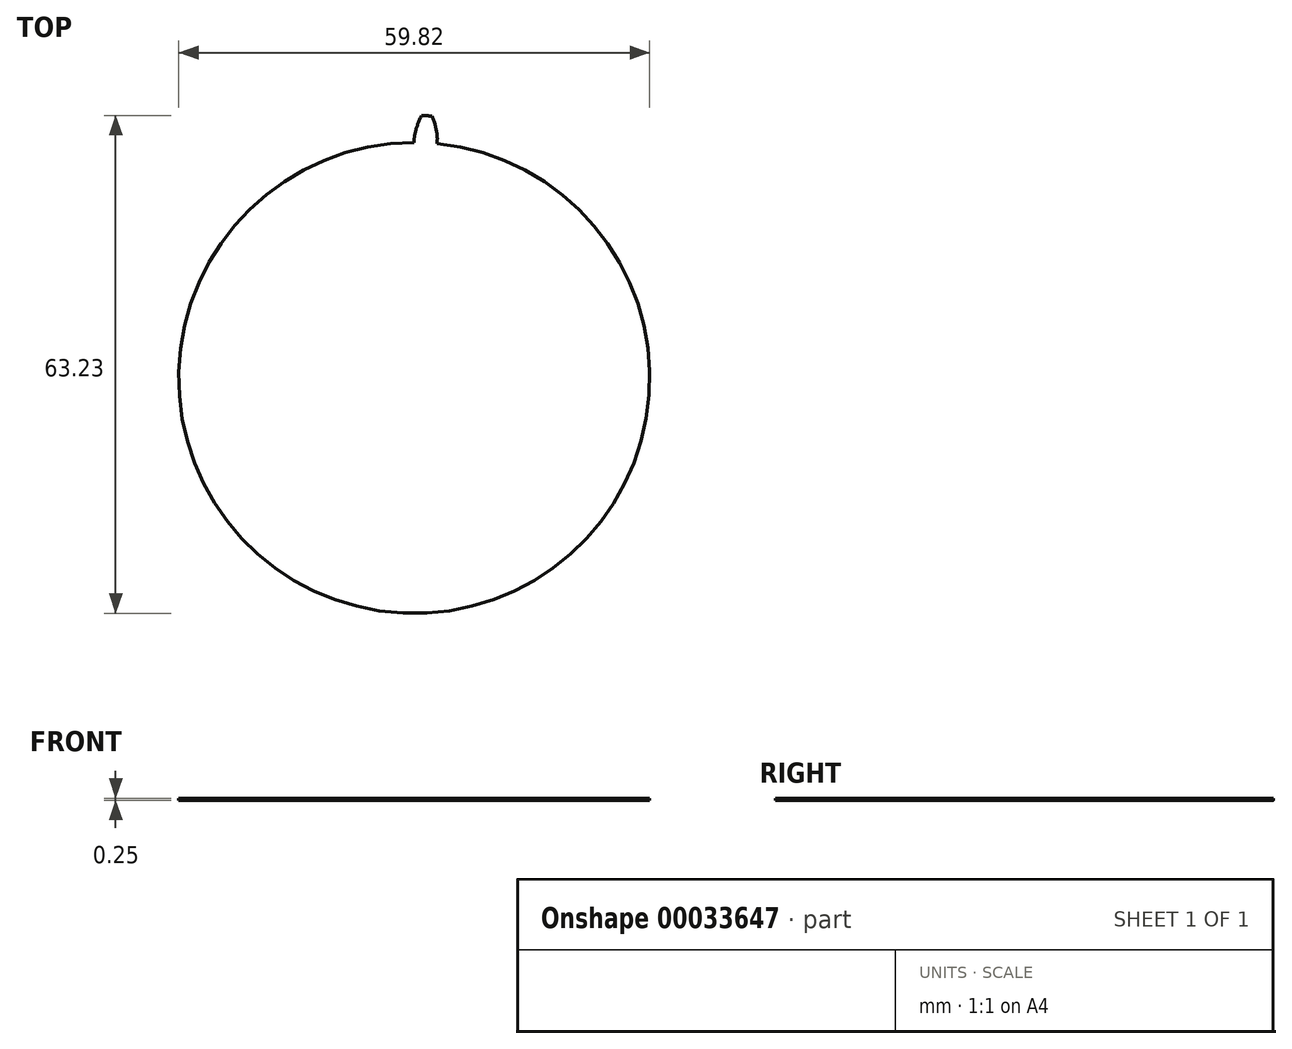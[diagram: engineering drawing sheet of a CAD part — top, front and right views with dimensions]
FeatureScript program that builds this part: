
annotation { "Feature Type Name" : "Feature", "Feature Type Description" : "" }
export const myFeature = defineFeature(function(context is Context, id is Id, definition is map)
    precondition{}
    {
        {
            assignVariable(context, id + "F0", {"name" : "N", "anyValue" : 16 * 2.5});
        }
        {
            assignVariable(context, id + "F1", {"name" : "Swid", "anyValue" : 0.25});
        }
        {
            var Q0;
            Q0=qCreatedBy(makeId("Top.planeOp"),FACE);
            var sketch = newSketch(context, id + "F2", { "sketchPlane" : qUnion([Q0])});
            skCircle(sketch, "E0", {"center": v(0, 0) * mm, "radius": 30.36 * mm, "construction": true});
            skCircle(sketch, "E1", {"center": v(0, 0) * mm, "radius": 31.75 * mm, "construction": true});
            skCircle(sketch, "E2", {"center": v(0, 0) * mm, "radius": 33.34 * mm});
            skLineSegment(sketch, "E3", {"start": v(0, 0) * mm, "end": v(0, 30.36) * mm, "construction": true});
            skLineSegment(sketch, "E4", {"start": v(0, 0) * mm, "end": v(1.99, 30.3) * mm, "construction": true});
            skLineSegment(sketch, "E5", {"start": v(0, 0) * mm, "end": v(3.96, 30.1) * mm, "construction": true});
            skLineSegment(sketch, "E6", {"start": v(0, 0) * mm, "end": v(5.92, 29.78) * mm, "construction": true});
            skLineSegment(sketch, "E7", {"start": v(0, 0) * mm, "end": v(7.86, 29.33) * mm, "construction": true});
            skCircle(sketch, "E8", {"center": v(0, 0) * mm, "radius": 29.91 * mm});
            skLineSegment(sketch, "E9", {"start": v(1.99, 30.3) * mm, "end": v(0, 30.43) * mm, "construction": true});
            skLineSegment(sketch, "E10", {"start": v(3.96, 30.1) * mm, "end": v(0.02, 30.62) * mm, "construction": true});
            skLineSegment(sketch, "E11", {"start": v(5.92, 29.78) * mm, "end": v(0.08, 30.94) * mm, "construction": true});
            skLineSegment(sketch, "E12", {"start": v(7.86, 29.33) * mm, "end": v(0.18, 31.39) * mm, "construction": true});
            skLineSegment(sketch, "E13", {"start": v(0, 0) * mm, "end": v(9.76, 28.75) * mm, "construction": true});
            skLineSegment(sketch, "E14", {"start": v(9.76, 28.75) * mm, "end": v(0.35, 31.95) * mm, "construction": true});
            skLineSegment(sketch, "E15", {"start": v(0, 0) * mm, "end": v(11.62, 28.05) * mm, "construction": true});
            skLineSegment(sketch, "E16", {"start": v(0, 0) * mm, "end": v(13.43, 27.23) * mm, "construction": true});
            skLineSegment(sketch, "E17", {"start": v(0, 0) * mm, "end": v(15.18, 26.3) * mm, "construction": true});
            skLineSegment(sketch, "E18", {"start": v(11.62, 28.05) * mm, "end": v(0.6, 32.61) * mm, "construction": true});
            skLineSegment(sketch, "E19", {"start": v(13.43, 27.23) * mm, "end": v(0.95, 33.38) * mm, "construction": true});
            skLineSegment(sketch, "E20", {"start": v(15.18, 26.3) * mm, "end": v(1.41, 34.24) * mm, "construction": true});
            skLineSegment(sketch, "E21", {"start": v(0, 0) * mm, "end": v(16.87, 25.25) * mm, "construction": true});
            skLineSegment(sketch, "E22", {"start": v(0, 0) * mm, "end": v(18.48, 24.09) * mm, "construction": true});
            skLineSegment(sketch, "E23", {"start": v(0, 0) * mm, "end": v(20.02, 22.83) * mm, "construction": true});
            skLineSegment(sketch, "E24", {"start": v(0, 0) * mm, "end": v(21.47, 21.47) * mm, "construction": true});
            skLineSegment(sketch, "E25", {"start": v(0, 0) * mm, "end": v(22.83, 20.02) * mm, "construction": true});
            skLineSegment(sketch, "E26", {"start": v(16.87, 25.25) * mm, "end": v(2, 35.18) * mm, "construction": true});
            skLineSegment(sketch, "E27", {"start": v(18.48, 24.09) * mm, "end": v(2.72, 36.19) * mm, "construction": true});
            skLineSegment(sketch, "E28", {"start": v(20.02, 22.83) * mm, "end": v(3.58, 37.24) * mm, "construction": true});
            skLineSegment(sketch, "E29", {"start": v(21.47, 21.47) * mm, "end": v(4.6, 38.33) * mm, "construction": true});
            skLineSegment(sketch, "E30", {"start": v(22.83, 20.02) * mm, "end": v(5.8, 39.44) * mm, "construction": true});
            skLineSegment(sketch, "E31", {"start": v(0, 0) * mm, "end": v(24.09, 18.48) * mm, "construction": true});
            skLineSegment(sketch, "E32", {"start": v(24.09, 18.48) * mm, "end": v(7.15, 40.56) * mm, "construction": true});
            skLineSegment(sketch, "E33", {"start": v(0, 0) * mm, "end": v(25.25, 16.87) * mm, "construction": true});
            skLineSegment(sketch, "E34", {"start": v(25.25, 16.87) * mm, "end": v(8.68, 41.65) * mm, "construction": true});
            skSolve(sketch);
        }
        {
            var Q0;
            Q0=qCreatedBy(makeId("Top.planeOp"),FACE);
            var sketch = newSketch(context, id + "F3", { "sketchPlane" : qUnion([Q0])});
            skLineSegment(sketch, "E35.0", {"start": v(24.09, 18.48) * mm, "end": v(7.15, 40.56) * mm, "construction": true});
            skLineSegment(sketch, "E35.1", {"start": v(22.83, 20.02) * mm, "end": v(5.8, 39.44) * mm, "construction": true});
            skLineSegment(sketch, "E35.2", {"start": v(21.47, 21.47) * mm, "end": v(4.6, 38.33) * mm, "construction": true});
            skLineSegment(sketch, "E35.3", {"start": v(20.02, 22.83) * mm, "end": v(3.58, 37.24) * mm, "construction": true});
            skLineSegment(sketch, "E35.4", {"start": v(18.48, 24.09) * mm, "end": v(2.72, 36.19) * mm, "construction": true});
            skLineSegment(sketch, "E35.5", {"start": v(16.87, 25.25) * mm, "end": v(2, 35.18) * mm, "construction": true});
            skLineSegment(sketch, "E35.6", {"start": v(15.18, 26.3) * mm, "end": v(1.41, 34.24) * mm, "construction": true});
            skLineSegment(sketch, "E35.7", {"start": v(13.43, 27.23) * mm, "end": v(0.95, 33.38) * mm, "construction": true});
            skLineSegment(sketch, "E35.8", {"start": v(11.62, 28.05) * mm, "end": v(0.6, 32.61) * mm, "construction": true});
            skLineSegment(sketch, "E35.9", {"start": v(9.76, 28.75) * mm, "end": v(0.35, 31.95) * mm, "construction": true});
            skLineSegment(sketch, "E35.10", {"start": v(7.86, 29.33) * mm, "end": v(0.18, 31.39) * mm, "construction": true});
            skLineSegment(sketch, "E35.11", {"start": v(5.92, 29.78) * mm, "end": v(0.08, 30.94) * mm, "construction": true});
            skLineSegment(sketch, "E35.12", {"start": v(3.96, 30.1) * mm, "end": v(0.02, 30.62) * mm, "construction": true});
            skLineSegment(sketch, "E35.13", {"start": v(1.99, 30.3) * mm, "end": v(0, 30.43) * mm, "construction": true});
            skCircle(sketch, "E35.14", {"center": v(0, 0) * mm, "radius": 30.36 * mm});
            skCircle(sketch, "E35.15", {"center": v(0, 0) * mm, "radius": 29.91 * mm});
            skCircle(sketch, "E35.16", {"center": v(0, 0) * mm, "radius": 31.75 * mm, "construction": true});
            skCircle(sketch, "E35.17", {"center": v(0, 0) * mm, "radius": 33.34 * mm});
            skLineSegment(sketch, "E36.0", {"start": v(25.25, 16.87) * mm, "end": v(8.68, 41.65) * mm, "construction": true});
            skLineSegment(sketch, "E37.0", {"start": v(0, 0) * mm, "end": v(0, 30.36) * mm, "construction": true});
            skFitSpline(sketch, "E38", {"points": [v(0, 30.36) * mm, v(0, 30.43) * mm, v(0.02, 30.62) * mm, v(0.08, 30.94) * mm, v(0.18, 31.39) * mm, v(0.35, 31.95) * mm, v(0.6, 32.61) * mm, v(0.95, 33.38) * mm, v(1.41, 34.24) * mm, v(2, 35.18) * mm, v(2.72, 36.19) * mm, v(3.58, 37.24) * mm, v(4.6, 38.33) * mm, v(5.8, 39.44) * mm, v(7.15, 40.56) * mm, v(8.68, 41.65) * mm, v(0, 0) * mm], "startDerivative": vector(0.68, 15.67) * mm, "endDerivative": vector(-81.92, -392.9) * mm});
            skLineSegment(sketch, "E39", {"start": v(0.29, 31.75) * mm, "end": v(0, 0) * mm, "construction": true});
            skLineSegment(sketch, "E40", {"start": v(0, 0) * mm, "end": v(1.6, 33.3) * mm, "construction": true});
            skFitSpline(sketch, "E41.MirrorCS", {"points": [v(2.93, 30.22) * mm, v(2.93, 30.29) * mm, v(2.93, 30.48) * mm, v(2.9, 30.8) * mm, v(2.85, 31.26) * mm, v(2.73, 31.83) * mm, v(2.54, 32.52) * mm, v(2.27, 33.32) * mm, v(1.9, 34.22) * mm, v(1.4, 35.21) * mm, v(0.78, 36.28) * mm, v(0.02, 37.41) * mm, v(-0.89, 38.6) * mm, v(-1.96, 39.82) * mm, v(-3.2, 41.06) * mm, v(-4.63, 42.3) * mm, v(0, 0) * mm], "startDerivative": vector(0.83, 15.67) * mm, "endDerivative": vector(43.65, -398.97) * mm});
            skLineSegment(sketch, "E42", {"start": v(2.93, 30.22) * mm, "end": v(2.88, 29.77) * mm});
            skLineSegment(sketch, "E43", {"start": v(0, 30.36) * mm, "end": v(0, 29.91) * mm});
            skSolve(sketch);
        }
        {
            var Q0;
            {var subQ3=sQuery(id+"F3.wireOp",EDGE,"E41.MirrorCS");var subQ6=sQuery(id+"F3.wireOp",EDGE,"E35.17");var subQ8=makeQuery(id+"F3.imprint","INTERSECT",VERTEX,{"disambiguationData":[OD(1.0)],"derivedFrom":[subQ6,subQ3]});Q0=makeQuery(id+"F3.imprint","IMPRINT",FACE,{"disambiguationData":[TD([[makeQuery(id+"F3.imprint","IMPRINT",EDGE,{"disambiguationData":[TD([[subQ8,-1.0]])],"derivedFrom":subQ6}),1.0]])]});}
            var Q1;
            {var subQ3=sQuery(id+"F3.wireOp",EDGE,"E41.MirrorCS");var subQ5=sQuery(id+"F3.wireOp",EDGE,"E35.15");var subQ6=makeQuery(id+"F3.imprint","INTERSECT",VERTEX,{"derivedFrom":[subQ5,subQ3]});Q1=makeQuery(id+"F3.imprint","IMPRINT",FACE,{"disambiguationData":[TD([[makeQuery(id+"F3.imprint","IMPRINT",EDGE,{"disambiguationData":[TD([[subQ6,-1.0]])],"derivedFrom":subQ5}),1.0]])]});}
            var Q2;
            {var subQ2=sQuery(id+"F3.wireOp",EDGE,"E42");Q2=makeQuery(id+"F3.imprint","IMPRINT",FACE,{"disambiguationData":[TD([[makeQuery(id+"F3.imprint","IMPRINT",EDGE,{"derivedFrom":subQ2}),-1.0]])]});}
            extrude(context, id + "F4", {"entities" : qUnion([Q0, Q1, Q2]), "depth" : (getVariable(context, 'Swid')) * mm, "offsetDistance" : 25.4 * mm});
        }
        {
            var Q0;
            Q0=qCreatedBy(makeId("Right.planeOp"),FACE);
            var sketch = newSketch(context, id + "F5", { "sketchPlane" : qUnion([Q0])});
            skLineSegment(sketch, "E44", {"start": v(0, 0) * mm, "end": v(0, 43.3) * mm, "construction": true});
            skSolve(sketch);
        }
        {
            var Q0;
            Q0=makeQuery(id+"F4.opExtrude","SWEPT_BODY",BODY,{"disambiguationData":[OSD([sQuery(id+"F3.wireOp",EDGE,"E35.15"),sQuery(id+"F3.wireOp",EDGE,"E35.17"),sQuery(id+"F3.wireOp",EDGE,"E38"),sQuery(id+"F3.wireOp",EDGE,"E41.MirrorCS"),sQuery(id+"F3.wireOp",EDGE,"9305e2c8-a00a-4cbc-a3b2-8fc88bc1717c"),sQuery(id+"F3.wireOp",EDGE,"f762f43d-eaf9-45ff-b6cd-062fd530227c")])]});
            var Q1;
            Q1=sQuery(id+"F5.wireOp",EDGE,"E44");
            circularPattern(context, id + "F6", {"operationType" : NewBodyOperationType.ADD, "entities" : qUnion([Q0]), "axis" : qUnion([Q1]), "angle" : (360 / getVariable(context, 'N')) * degree, "instanceCount" : getVariable(context, 'N'), "oppositeDirection" : true});
        }
    });
